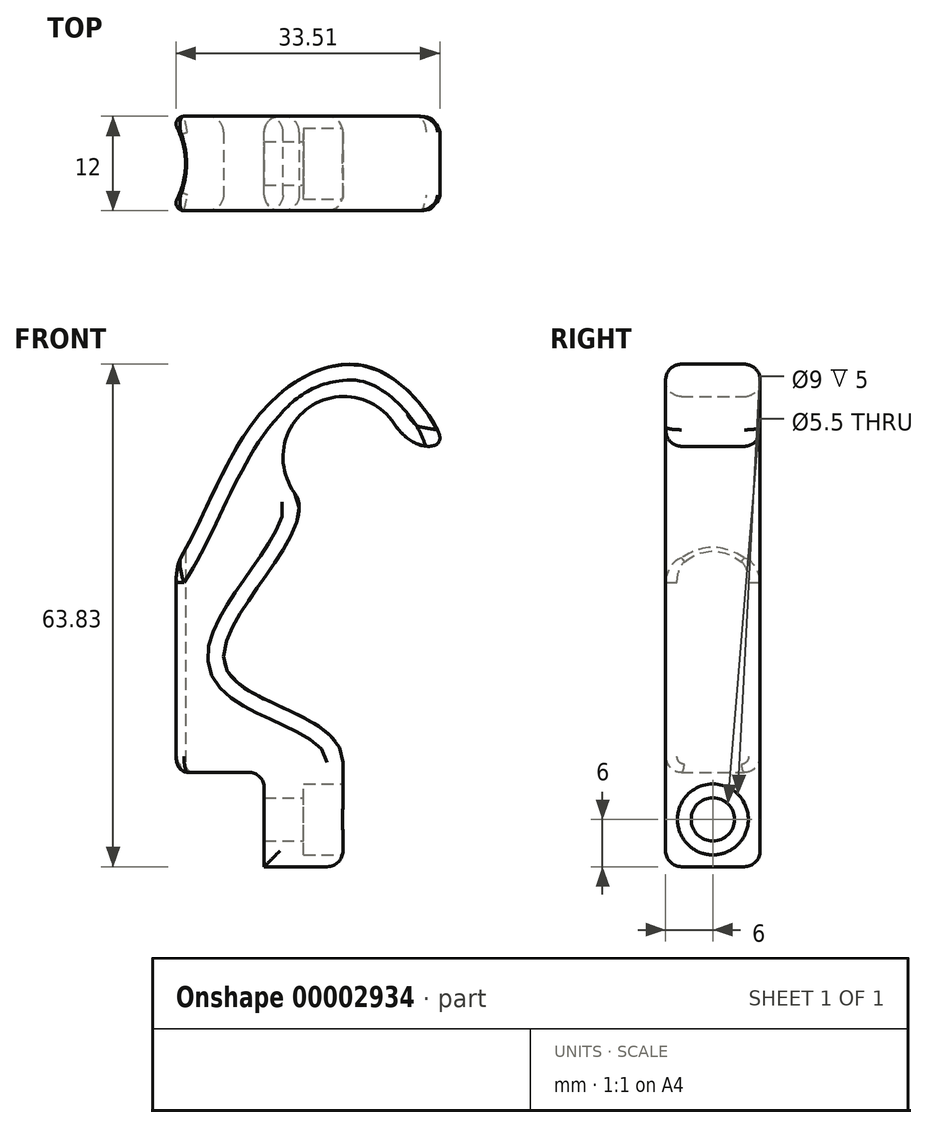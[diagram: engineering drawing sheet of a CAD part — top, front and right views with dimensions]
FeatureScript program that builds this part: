
annotation { "Feature Type Name" : "Feature", "Feature Type Description" : "" }
export const myFeature = defineFeature(function(context is Context, id is Id, definition is map)
    precondition{}
    {
        {
            var Q0;
            Q0=qCreatedBy(makeId("Front.planeOp"),FACE);
            var sketch = newSketch(context, id + "F0", { "sketchPlane" : qUnion([Q0])});
            skLineSegment(sketch, "E0", {"start": v(0, 0) * mm, "end": v(10, 0) * mm});
            skLineSegment(sketch, "E1", {"start": v(10, 13.25) * mm, "end": v(10, 0) * mm});
            skArc(sketch, "E2", {"start": v(16.5, 56.27) * mm, "mid": v(5.7, 58.35) * mm, "end": v(3.86, 47.5) * mm});
            skLineSegment(sketch, "E3", {"start": v(-18.38, 21.32) * mm, "end": v(-18.38, 12) * mm});
            skLineSegment(sketch, "E4", {"start": v(-18.38, 12) * mm, "end": v(0, 12) * mm});
            skLineSegment(sketch, "E5", {"start": v(0, 12) * mm, "end": v(0, 0) * mm});
            skFitSpline(sketch, "E6", {"points": [v(16.5, 56.27) * mm, v(22.05, 53.77) * mm, v(21.58, 56.27) * mm, v(13.24, 63.51) * mm, v(0, 58.15) * mm, v(-10.76, 38.99) * mm, v(-18.38, 21.32) * mm], "startDerivative": vector(50.23, -75.87) * mm, "endDerivative": vector(-10.85, -130.45) * mm});
            skFitSpline(sketch, "E7", {"points": [v(3.86, 47.5) * mm, v(-5.09, 25.82) * mm, v(10, 13.25) * mm], "startDerivative": vector(20.38, -28.05) * mm, "endDerivative": vector(0, -40.08) * mm});
            skSolve(sketch);
        }
        {
            var Q0;
            Q0=makeQuery(id+"F0.imprint","IMPRINT",FACE,{"disambiguationData":[TD([[makeQuery(id+"F0.imprint","IMPRINT",EDGE,{"derivedFrom":sQuery(id+"F0.wireOp",EDGE,"E0")}),1.0]])]});
            extrude(context, id + "F1", {"entities" : qUnion([Q0]), "depth" : 12 * mm});
        }
        {
            var Q0;
            Q0=qCreatedBy(makeId("Top.planeOp"),FACE);
            var sketch = newSketch(context, id + "F2", { "sketchPlane" : qUnion([Q0])});
            skCircle(sketch, "E8", {"center": v(-20, -6) * mm, "radius": 10 * mm});
            skPoint(sketch, "E9.end.orphan", {"position": v(0, -6) * mm});
            skPoint(sketch, "E9.start.orphan", {"position": v(0, 8.32) * mm});
            skSolve(sketch);
        }
        {
            var Q0;
            Q0=makeQuery(id+"F1.opExtrude","CAP_FACE",FACE,{"disambiguationData":[OSD([sQuery(id+"F0.wireOp",EDGE,"E0"),sQuery(id+"F0.wireOp",EDGE,"E1"),sQuery(id+"F0.wireOp",EDGE,"2e3813e5-8b83-4872-b0e6-d82be675f64c"),sQuery(id+"F0.wireOp",EDGE,"3e9490e4-665b-4c3a-a155-6cc6a639aaf7"),sQuery(id+"F0.wireOp",EDGE,"b3834555-f281-4aa2-b6ea-c9b1417e00d6"),sQuery(id+"F0.wireOp",EDGE,"E2"),sQuery(id+"F0.wireOp",EDGE,"E3"),sQuery(id+"F0.wireOp",EDGE,"E4"),sQuery(id+"F0.wireOp",EDGE,"E5"),sQuery(id+"F0.wireOp",EDGE,"95b372bf-4945-426e-b6ba-0a7f2843703d.filletArc"),sQuery(id+"F0.wireOp",EDGE,"55c0f577-1c56-42e2-ac56-c2b664ff22a2.filletArc")])],"isStart":false});
            var Q1;
            Q1=makeQuery(id+"F1.opExtrude","CAP_FACE",FACE,{"disambiguationData":[OSD([sQuery(id+"F0.wireOp",EDGE,"E0"),sQuery(id+"F0.wireOp",EDGE,"E1"),sQuery(id+"F0.wireOp",EDGE,"2e3813e5-8b83-4872-b0e6-d82be675f64c"),sQuery(id+"F0.wireOp",EDGE,"3e9490e4-665b-4c3a-a155-6cc6a639aaf7"),sQuery(id+"F0.wireOp",EDGE,"b3834555-f281-4aa2-b6ea-c9b1417e00d6"),sQuery(id+"F0.wireOp",EDGE,"E2"),sQuery(id+"F0.wireOp",EDGE,"E3"),sQuery(id+"F0.wireOp",EDGE,"E4"),sQuery(id+"F0.wireOp",EDGE,"E5"),sQuery(id+"F0.wireOp",EDGE,"95b372bf-4945-426e-b6ba-0a7f2843703d.filletArc"),sQuery(id+"F0.wireOp",EDGE,"55c0f577-1c56-42e2-ac56-c2b664ff22a2.filletArc")])],"isStart":true});
            var Q2;
            Q2=makeQuery(id+"F1.opExtrude","SWEPT_FACE",FACE,{"disambiguationData":[OSD([sQuery(id+"F0.wireOp",EDGE,"E1")])]});
            var Q3;
            Q3=makeQuery(id+"F1.opExtrude","SWEPT_FACE",FACE,{"disambiguationData":[OSD([sQuery(id+"F0.wireOp",EDGE,"E4")])]});
            fillet(context, id + "F3", {"entities" : qUnion([Q0, Q1, Q2, Q3]), "radius" : 2 * mm, "allowEdgeOverflow" : false});
        }
        {
            var Q0;
            Q0=makeQuery(id+"F1.opExtrude","SWEPT_FACE",FACE,{"disambiguationData":[OSD([sQuery(id+"F0.wireOp",EDGE,"E1")])]});
            var sketch = newSketch(context, id + "F4", { "sketchPlane" : qUnion([Q0])});
            skCircle(sketch, "E10", {"center": v(-6, 6) * mm, "radius": 4.5 * mm});
            skSolve(sketch);
        }
        {
            var Q0;
            Q0 = qSketchRegion(id + "F4", true);
            extrude(context, id + "F5", {"entities" : qUnion([Q0]), "operationType" : NewBodyOperationType.REMOVE, "oppositeDirection" : true, "depth" : 5 * mm});
        }
        {
            var Q0;
            Q0=makeQuery(id+"F1.opExtrude","SWEPT_FACE",FACE,{"disambiguationData":[OSD([sQuery(id+"F0.wireOp",EDGE,"E1")])]});
            var sketch = newSketch(context, id + "F6", { "sketchPlane" : qUnion([Q0])});
            skCircle(sketch, "E11", {"center": v(-6, 6) * mm, "radius": 2.75 * mm});
            skSolve(sketch);
        }
        {
            var Q0;
            Q0=makeQuery(id+"F6.imprint","IMPRINT",FACE,{"disambiguationData":[TD([[makeQuery(id+"F6.imprint","IMPRINT",EDGE,{"derivedFrom":sQuery(id+"F6.wireOp",EDGE,"E11")}),1.0]])]});
            extrude(context, id + "F7", {"entities" : qUnion([Q0]), "operationType" : NewBodyOperationType.REMOVE, "oppositeDirection" : true, "depth" : 25 * mm});
        }
        {
            var Q0;
            Q0=makeQuery(id+"F2.imprint","IMPRINT",FACE,{"disambiguationData":[TD([[makeQuery(id+"F2.imprint","IMPRINT",EDGE,{"derivedFrom":sQuery(id+"F2.wireOp",EDGE,"E8")}),1.0]])]});
            extrude(context, id + "F8", {"entities" : qUnion([Q0]), "operationType" : NewBodyOperationType.REMOVE, "depth" : 50 * mm});
        }
        {
            var Q0;
            Q0=makeQuery(id+"F8.boolean.opBoolean","COPY",FACE,{"derivedFrom":makeQuery(id+"F8.opExtrude","SWEPT_FACE",FACE,{"disambiguationData":[OSD([sQuery(id+"F2.wireOp",EDGE,"E8")])]})});
            fillet(context, id + "F9", {"entities" : qUnion([Q0]), "radius" : 1 * mm, "tangentPropagation" : true, "allowEdgeOverflow" : false});
        }
    });
